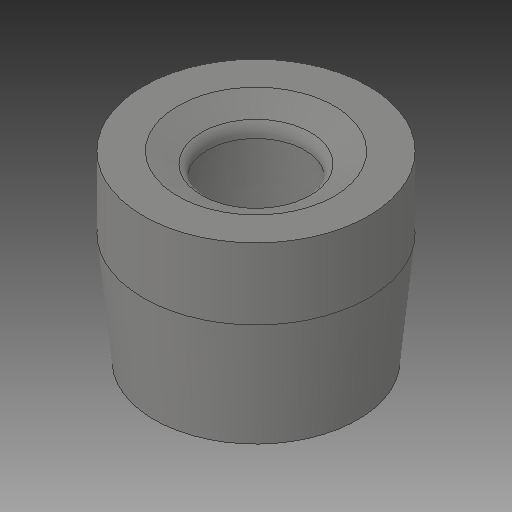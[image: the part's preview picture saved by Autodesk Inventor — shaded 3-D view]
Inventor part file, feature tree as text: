
AUTODESK INVENTOR PART (.ipt)
format: ipt  version: 2017 (Build 210142000, 142)  size: 192,000 bytes
history: native  units: in
note: dims shown in document units (in); Inventor stores cm internally (conversion verified against a paired STEP export)
features: revolve x1, sketch x1
ambient origin geometry x8: Origin, YZ Plane, XZ Plane, XY Plane, X Axis, Y Axis, Z Axis, Center Point
bodies: Body1 (feature_tree)
feature tree (2):
  revolve  "Revolution2"  [1 undecoded]
  sketch  "Sketch1"  dims[d0=1.13in d1=3.75in d2=0.125in d3=0.1718in d5=1.0in d6=1.0in d7=90.0deg d8=0.5in d9=15.0deg d12=1.25in d13=0.25in d16=0.5in d17=0.5in d18=0.5in d19=2.5in d20=0.5in d22=0.375in d23=0.25in d25=0.234in d27=0.125in d28=0.25in d29=1.0in d30=4.25in d31=0.25in d33=0.8014in d34=15.0deg d35=0.125in d36=1.0in d38=90.0deg]
note: 1 required parameter value undecoded (feature->parameter linkage not recoverable at this tier; creation-order binding heuristic only, values carry confidence <= 0.55)
